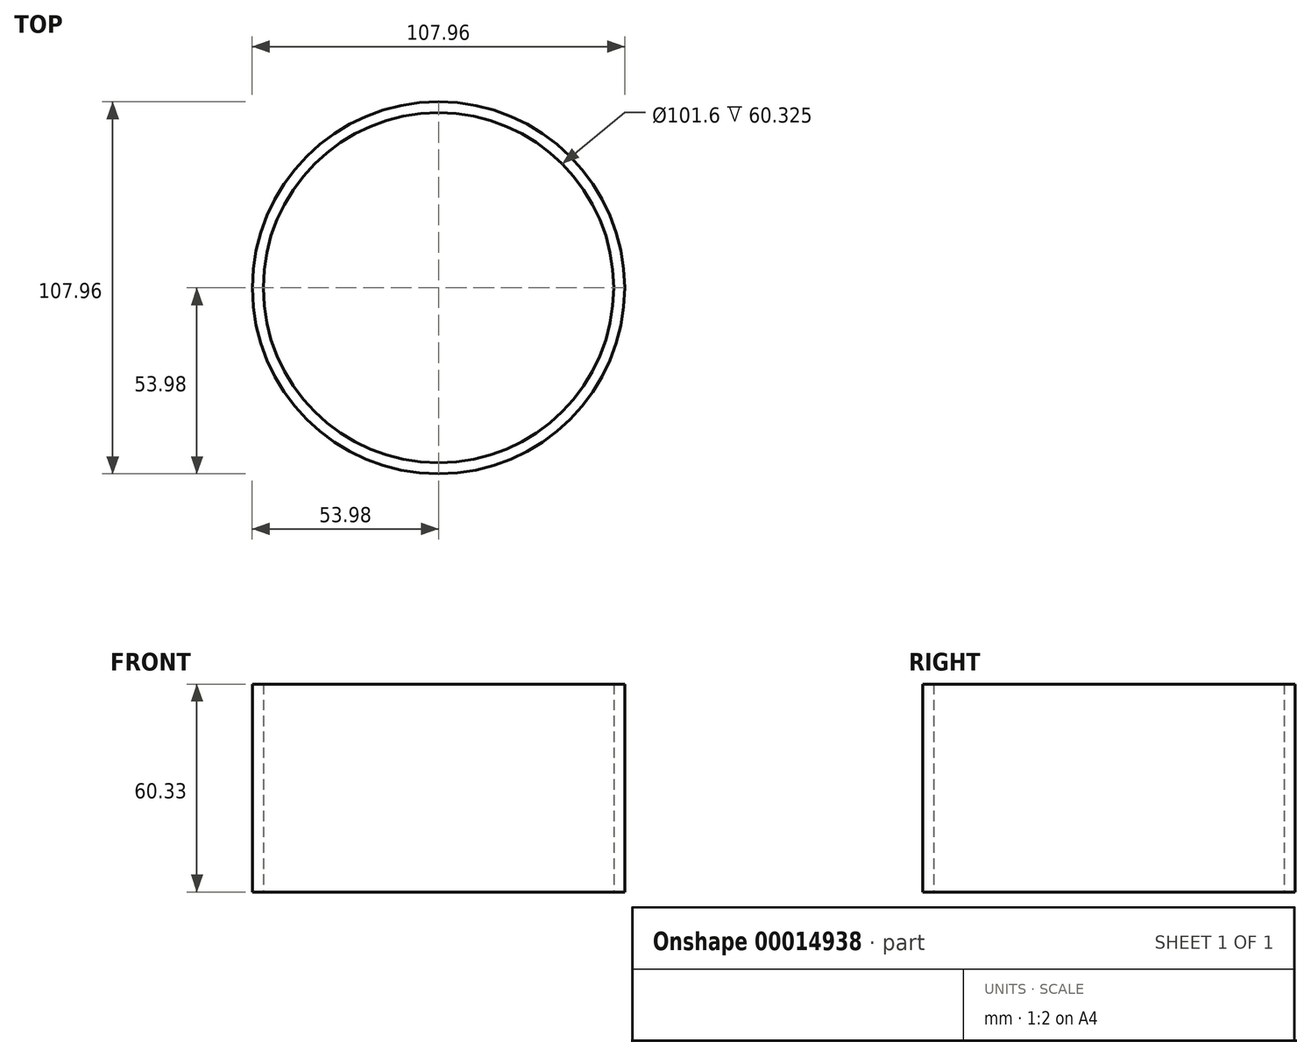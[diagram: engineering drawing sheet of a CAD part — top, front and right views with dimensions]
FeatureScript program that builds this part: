
annotation { "Feature Type Name" : "Feature", "Feature Type Description" : "" }
export const myFeature = defineFeature(function(context is Context, id is Id, definition is map)
    precondition{}
    {
        {
            var Q0;
            Q0=qCreatedBy(makeId("Top.planeOp"),FACE);
            var sketch = newSketch(context, id + "F0", { "sketchPlane" : qUnion([Q0])});
            skCircle(sketch, "E0", {"center": v(0, 0) * mm, "radius": 50.8 * mm});
            skCircle(sketch, "E1", {"center": v(0, 0) * mm, "radius": 53.98 * mm});
            skSolve(sketch);
        }
        {
            var Q0;
            Q0=makeQuery(id+"F0.imprint","IMPRINT",FACE,{"disambiguationData":[TD([[makeQuery(id+"F0.imprint","IMPRINT",EDGE,{"derivedFrom":sQuery(id+"F0.wireOp",EDGE,"E0")}),-1.0]])]});
            extrude(context, id + "F1", {"entities" : qUnion([Q0]), "depth" : 60.32 * mm});
        }
    });
